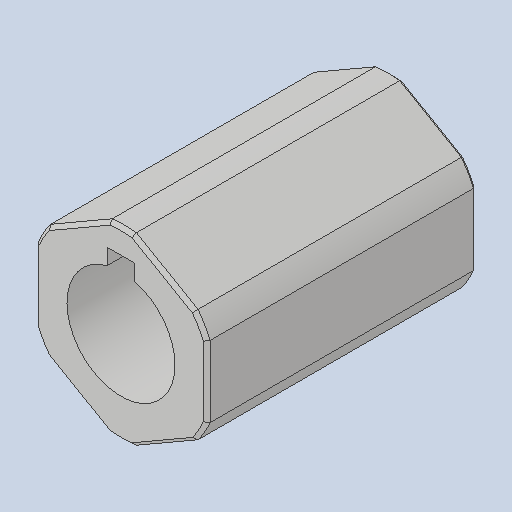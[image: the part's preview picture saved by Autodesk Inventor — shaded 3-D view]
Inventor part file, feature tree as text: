
AUTODESK INVENTOR PART (.ipt)
format: ipt  version: 2023.3 (Build 273359000, 359)  size: 127,488 bytes
history: native  units: in
note: dims shown in document units (in); Inventor stores cm internally (conversion verified against a paired STEP export)
features: chamfer x1
ambient origin geometry x8: Origin, YZ Plane, XZ Plane, XY Plane, X Axis, Y Axis, Z Axis, Center Point
bodies: Solid1 (feature_tree)
feature tree (1):
  chamfer  "Chamfer1"  [1 undecoded]
note: 1 required parameter value undecoded (feature->parameter linkage not recoverable at this tier; creation-order binding heuristic only, values carry confidence <= 0.55)
